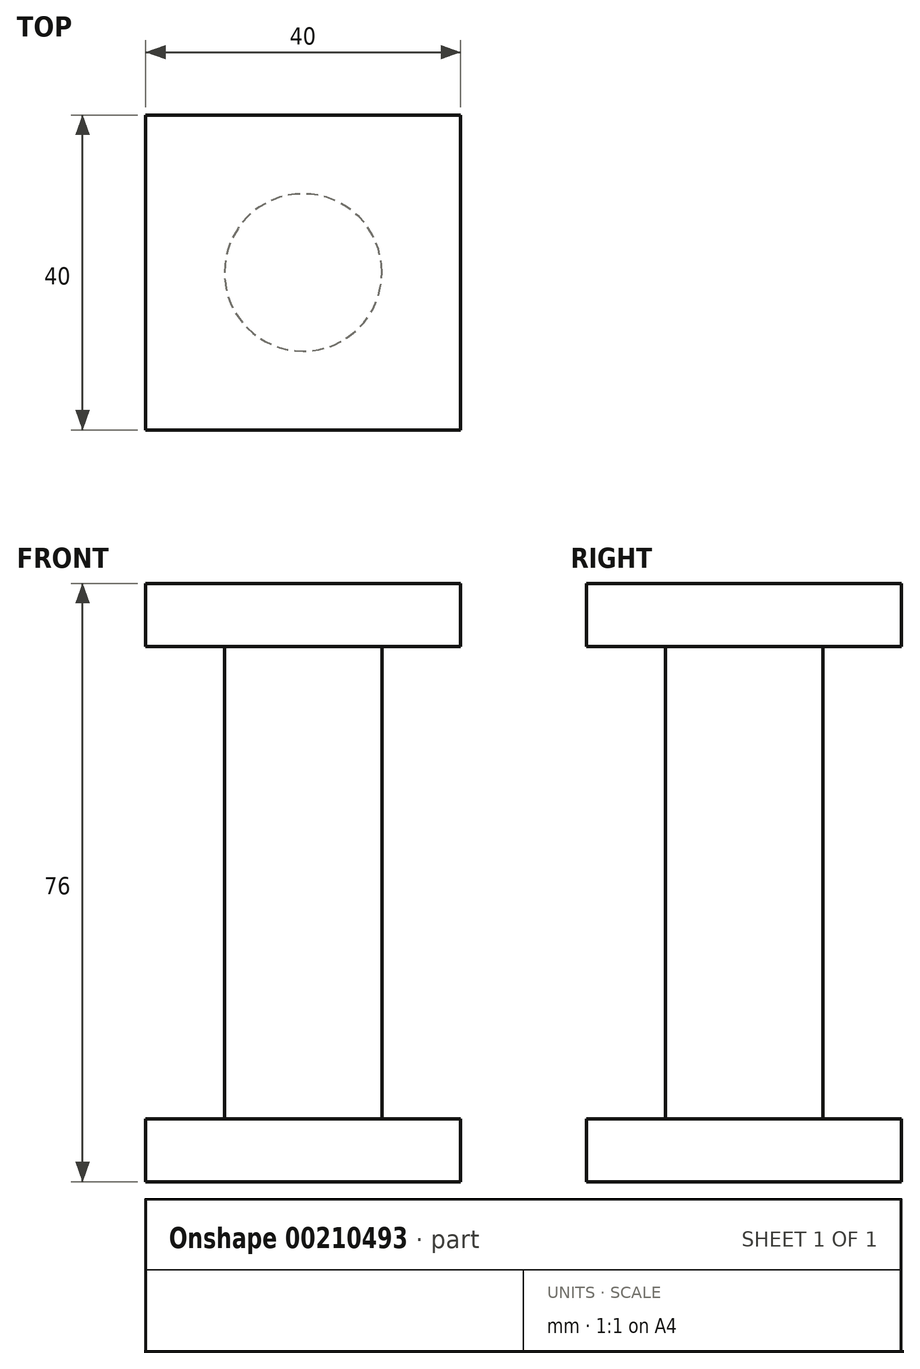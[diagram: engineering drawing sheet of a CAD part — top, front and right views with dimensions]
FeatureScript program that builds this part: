
annotation { "Feature Type Name" : "Feature", "Feature Type Description" : "" }
export const myFeature = defineFeature(function(context is Context, id is Id, definition is map)
    precondition{}
    {
        {
            var Q0;
            Q0=qCreatedBy(makeId("Front.planeOp"),FACE);
            var sketch = newSketch(context, id + "F0", { "sketchPlane" : qUnion([Q0])});
            skLineSegment(sketch, "E0.rect.bottom", {"start": v(-20, 4) * mm, "end": v(20, 4) * mm});
            skLineSegment(sketch, "E0.rect.top", {"start": v(-20, -4) * mm, "end": v(20, -4) * mm});
            skLineSegment(sketch, "E0.rect.left", {"start": v(-20, 4) * mm, "end": v(-20, -4) * mm});
            skLineSegment(sketch, "E0.rect.right", {"start": v(20, 4) * mm, "end": v(20, -4) * mm});
            skPoint(sketch, "E0.rect.middle", {"position": v(0, 0) * mm});
            skLineSegment(sketch, "E1.rect.bottom", {"start": v(-20, 64) * mm, "end": v(20, 64) * mm});
            skLineSegment(sketch, "E1.rect.top", {"start": v(-20, 72) * mm, "end": v(20, 72) * mm});
            skLineSegment(sketch, "E1.rect.left", {"start": v(-20, 64) * mm, "end": v(-20, 72) * mm});
            skLineSegment(sketch, "E1.rect.right", {"start": v(20, 64) * mm, "end": v(20, 72) * mm});
            skPoint(sketch, "E1.rect.middle", {"position": v(0, 68) * mm});
            skSolve(sketch);
        }
        {
            var Q0;
            Q0=qSketchRegion(id+"F0",true);
            extrude(context, id + "F1", {"entities" : qUnion([Q0]), "depth" : 40 * mm, "symmetric" : true});
        }
        {
            var Q0;
            Q0=makeQuery(id+"F1.opExtrude","SWEPT_FACE",FACE,{"disambiguationData":[OSD([sQuery(id+"F0.wireOp",EDGE,"E0.rect.bottom")])]});
            var sketch = newSketch(context, id + "F2", { "sketchPlane" : qUnion([Q0])});
            skCircle(sketch, "E2", {"center": v(0, 0) * mm, "radius": 10 * mm});
            skSolve(sketch);
        }
        {
            var Q0;
            Q0=qSketchRegion(id+"F2",true);
            var Q1;
            Q1=makeQuery(id+"F1.opExtrude","SWEPT_BODY",BODY,{"disambiguationData":[OSD([sQuery(id+"F0.wireOp",EDGE,"E1.rect.bottom"),sQuery(id+"F0.wireOp",EDGE,"E1.rect.top"),sQuery(id+"F0.wireOp",EDGE,"E1.rect.left"),sQuery(id+"F0.wireOp",EDGE,"E1.rect.right")])]});
            extrude(context, id + "F3", {"entities" : qUnion([Q0]), "endBound" : BoundingType.UP_TO_BODY, "endBoundEntityBody" : qUnion([Q1]), "depth" : 25 * mm});
        }
    });
